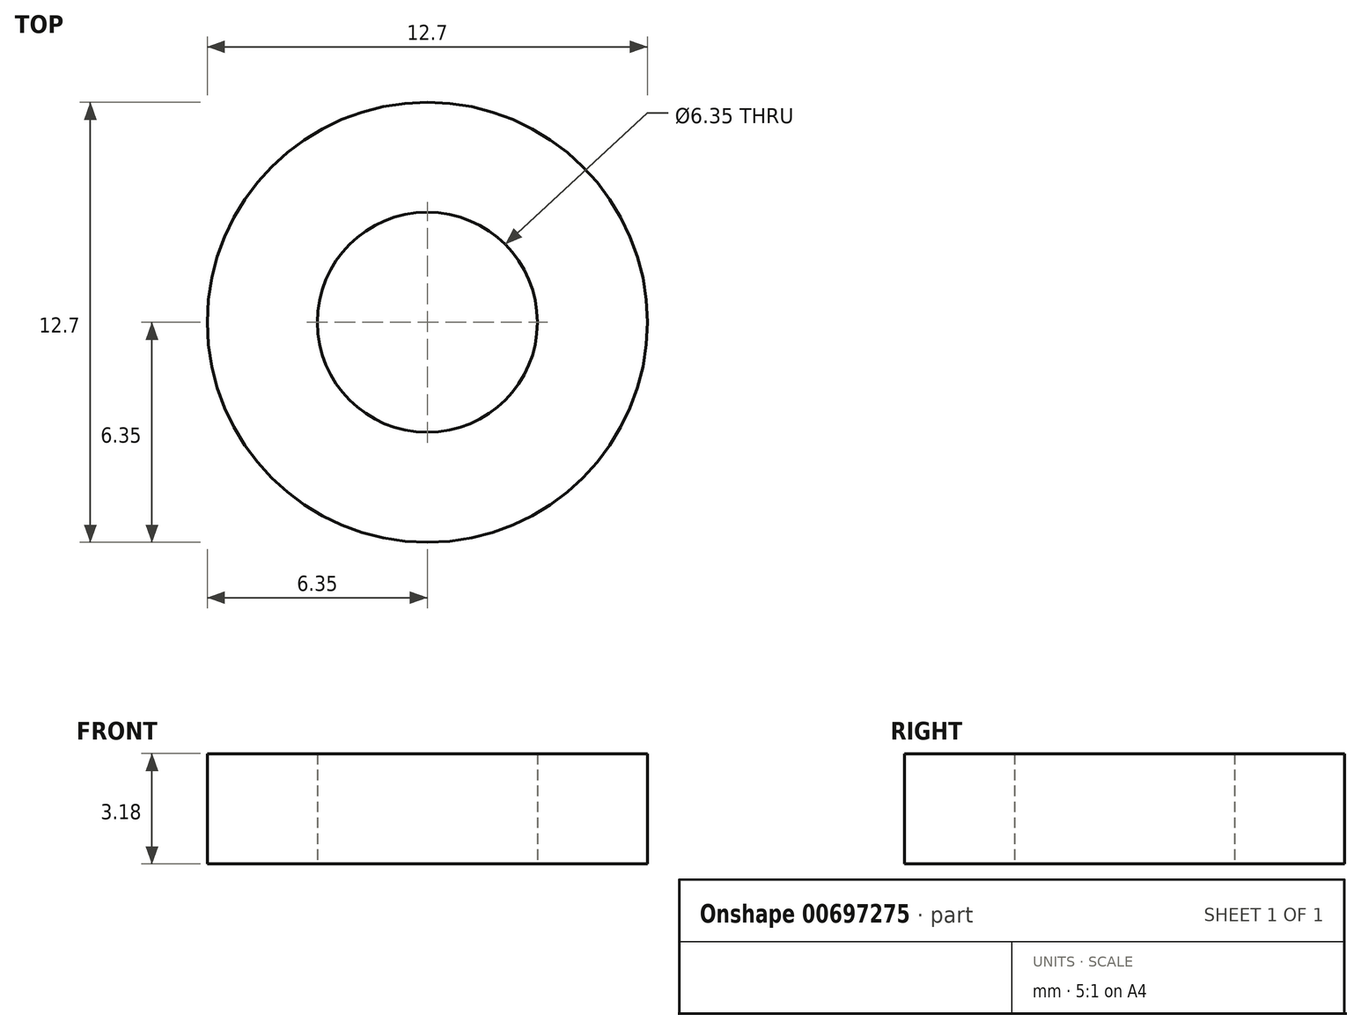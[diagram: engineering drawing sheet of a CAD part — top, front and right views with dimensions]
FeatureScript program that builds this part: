
annotation { "Feature Type Name" : "Feature", "Feature Type Description" : "" }
export const myFeature = defineFeature(function(context is Context, id is Id, definition is map)
    precondition{}
    {
        {
            var Q0;
            Q0=qCreatedBy(makeId("Top.planeOp"),FACE);
            var sketch = newSketch(context, id + "F0", { "sketchPlane" : qUnion([Q0])});
            skCircle(sketch, "E0", {"center": v(0, 0) * mm, "radius": 6.35 * mm});
            skCircle(sketch, "E1", {"center": v(0, 0) * mm, "radius": 3.17 * mm});
            skSolve(sketch);
        }
        {
            var Q0;
            Q0=makeQuery(id+"F0.imprint","IMPRINT",FACE,{"disambiguationData":[TD([[makeQuery(id+"F0.imprint","IMPRINT",EDGE,{"derivedFrom":sQuery(id+"F0.wireOp",EDGE,"E0")}),1.0]])]});
            extrude(context, id + "F1", {"entities" : qUnion([Q0]), "depth" : 3.17 * mm, "offsetDistance" : 25 * mm});
        }
    });
